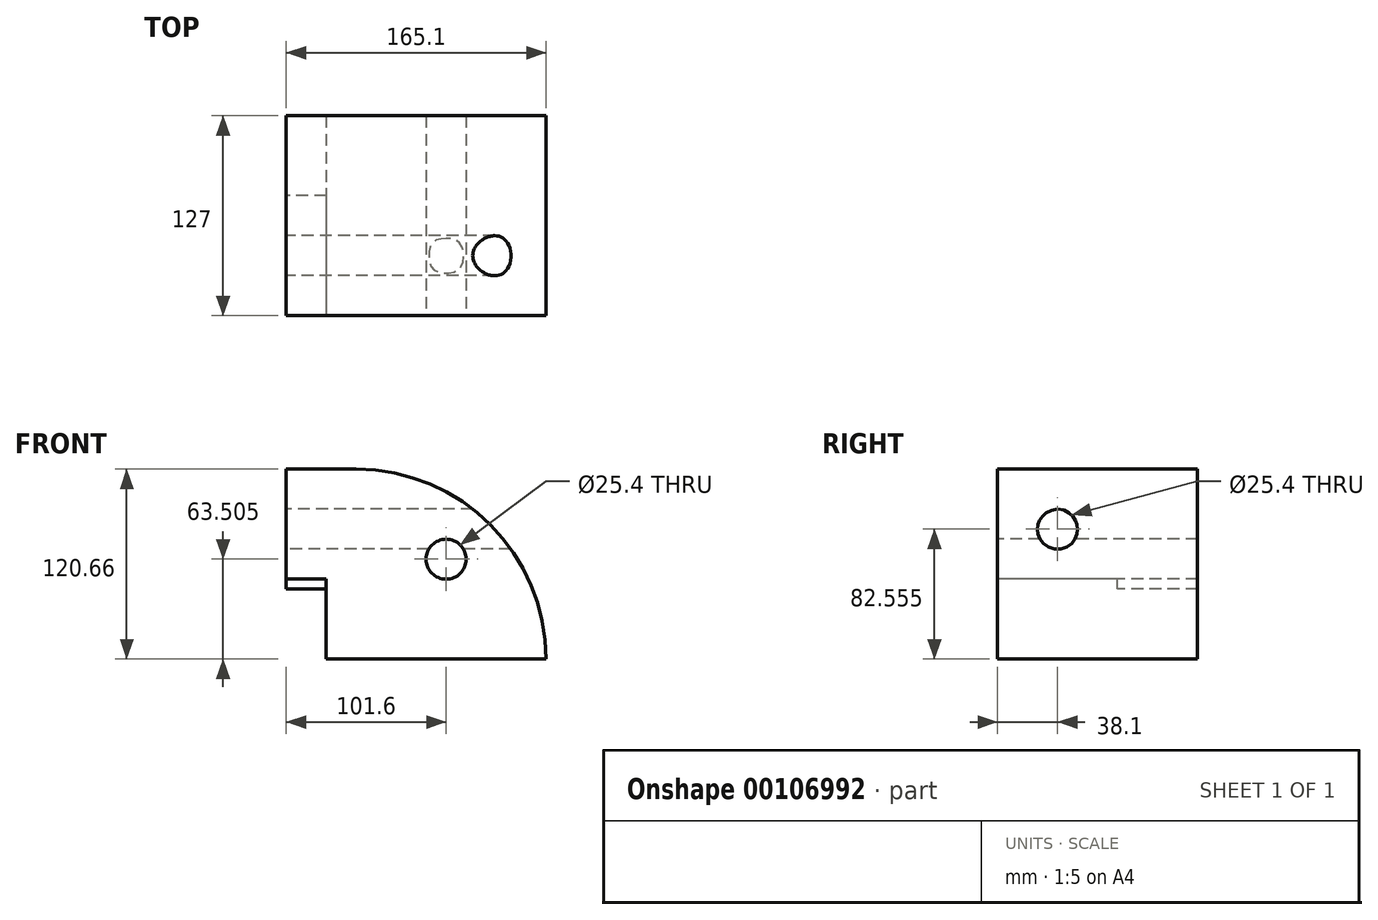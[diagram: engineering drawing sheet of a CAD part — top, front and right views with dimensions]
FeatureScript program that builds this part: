
annotation { "Feature Type Name" : "Feature", "Feature Type Description" : "" }
export const myFeature = defineFeature(function(context is Context, id is Id, definition is map)
    precondition{}
    {
        {
            var Q0;
            Q0=qCreatedBy(makeId("Right.planeOp"),FACE);
            var sketch = newSketch(context, id + "F0", { "sketchPlane" : qUnion([Q0])});
            skLineSegment(sketch, "E0.bottom", {"start": v(-63.5, 60.33) * mm, "end": v(63.5, 60.33) * mm});
            skLineSegment(sketch, "E0.top", {"start": v(-63.5, -60.33) * mm, "end": v(63.5, -60.33) * mm});
            skLineSegment(sketch, "E0.left", {"start": v(-63.5, 60.33) * mm, "end": v(-63.5, -60.33) * mm});
            skLineSegment(sketch, "E0.right", {"start": v(63.5, 60.32) * mm, "end": v(63.5, -60.33) * mm});
            skPoint(sketch, "E0.middle", {"position": v(0, 0) * mm});
            skSolve(sketch);
        }
        {
            var Q0;
            Q0=makeQuery(id+"F0.imprint","IMPRINT",FACE,{"disambiguationData":[TD([[makeQuery(id+"F0.imprint","IMPRINT",EDGE,{"derivedFrom":sQuery(id+"F0.wireOp",EDGE,"E0.bottom")}),-1.0]])]});
            extrude(context, id + "F1", {"entities" : qUnion([Q0]), "depth" : 215.9 * mm});
        }
        {
            var Q0;
            Q0=makeQuery(id+"F1.opExtrude","SWEPT_FACE",FACE,{"disambiguationData":[OSD([sQuery(id+"F0.wireOp",EDGE,"E0.left")])]});
            var sketch = newSketch(context, id + "F2", { "sketchPlane" : qUnion([Q0])});
            skLineSegment(sketch, "E1.bottom", {"start": v(0, -60.33) * mm, "end": v(76.2, -60.33) * mm});
            skLineSegment(sketch, "E1.top", {"start": v(0, -15.88) * mm, "end": v(76.2, -15.88) * mm});
            skLineSegment(sketch, "E1.left", {"start": v(0, -60.33) * mm, "end": v(0, -15.88) * mm});
            skLineSegment(sketch, "E1.right", {"start": v(76.2, -60.33) * mm, "end": v(76.2, -15.88) * mm});
            skSolve(sketch);
        }
        {
            var Q0;
            Q0=makeQuery(id+"F2.imprint","IMPRINT",FACE,{"disambiguationData":[TD([[makeQuery(id+"F2.imprint","IMPRINT",EDGE,{"derivedFrom":sQuery(id+"F2.wireOp",EDGE,"E1.bottom")}),-1.0]])]});
            extrude(context, id + "F3", {"entities" : qUnion([Q0]), "operationType" : NewBodyOperationType.REMOVE, "oppositeDirection" : true, "depth" : 127 * mm});
        }
        {
            var Q0;
            Q0=makeQuery(id+"F1.opExtrude","CAP_FACE",FACE,{"disambiguationData":[OSD([sQuery(id+"F0.wireOp",EDGE,"E0.bottom"),sQuery(id+"F0.wireOp",EDGE,"E0.top"),sQuery(id+"F0.wireOp",EDGE,"E0.left"),sQuery(id+"F0.wireOp",EDGE,"E0.right")])],"isStart":true});
            var sketch = newSketch(context, id + "F4", { "sketchPlane" : qUnion([Q0])});
            skLineSegment(sketch, "E2.bottom", {"start": v(-63.5, 60.32) * mm, "end": v(-12.7, 60.32) * mm});
            skLineSegment(sketch, "E2.top", {"start": v(-63.5, -15.88) * mm, "end": v(-12.7, -15.88) * mm});
            skLineSegment(sketch, "E2.left", {"start": v(-63.5, 60.32) * mm, "end": v(-63.5, -15.88) * mm});
            skLineSegment(sketch, "E2.right", {"start": v(-12.7, 60.32) * mm, "end": v(-12.7, -15.88) * mm});
            skLineSegment(sketch, "E3.bottom", {"start": v(-63.5, -15.88) * mm, "end": v(63.5, -15.88) * mm});
            skLineSegment(sketch, "E3.top", {"start": v(-63.5, -15.88) * mm, "end": v(63.5, -15.88) * mm});
            skLineSegment(sketch, "E3.left", {"start": v(-63.5, -15.88) * mm, "end": v(-63.5, -15.88) * mm});
            skLineSegment(sketch, "E3.right", {"start": v(63.5, -15.88) * mm, "end": v(63.5, -15.87) * mm});
            skSolve(sketch);
        }
        {
            var Q0;
            Q0=makeQuery(id+"F4.imprint","IMPRINT",FACE,{"disambiguationData":[TD([[makeQuery(id+"F4.imprint","IMPRINT",EDGE,{"derivedFrom":sQuery(id+"F4.wireOp",EDGE,"E2.bottom")}),1.0]])]});
            extrude(context, id + "F5", {"entities" : qUnion([Q0]), "operationType" : NewBodyOperationType.REMOVE, "oppositeDirection" : true, "depth" : 50.8 * mm});
        }
        {
            var Q0;
            Q0=makeQuery(id+"F1.opExtrude","CAP_FACE",FACE,{"disambiguationData":[OSD([sQuery(id+"F0.wireOp",EDGE,"E0.bottom"),sQuery(id+"F0.wireOp",EDGE,"E0.top"),sQuery(id+"F0.wireOp",EDGE,"E0.left"),sQuery(id+"F0.wireOp",EDGE,"E0.right")])],"isStart":true});
            var sketch = newSketch(context, id + "F6", { "sketchPlane" : qUnion([Q0])});
            skCircle(sketch, "E4", {"center": v(25.4, 22.22) * mm, "radius": 12.7 * mm});
            skSolve(sketch);
        }
        {
            var Q0;
            Q0=makeQuery(id+"F1.opExtrude","SWEPT_FACE",FACE,{"disambiguationData":[OSD([sQuery(id+"F0.wireOp",EDGE,"E0.left")])]});
            var sketch = newSketch(context, id + "F7", { "sketchPlane" : qUnion([Q0])});
            skLineSegment(sketch, "E5.bottom", {"start": v(215.9, -60.33) * mm, "end": v(141.2, -60.33) * mm});
            skLineSegment(sketch, "E5.left", {"start": v(215.9, -60.33) * mm, "end": v(215.9, -8.03) * mm});
            skPoint(sketch, "E6", {"position": v(152.4, 3.17) * mm});
            skSolve(sketch);
        }
        {
            var Q0;
            Q0=sQuery(id+"F7.wireOp",VERTEX,"E6");
            var Q1;
            Q1=makeQuery(id+"F1.opExtrude","SWEPT_BODY",BODY,{"disambiguationData":[OSD([sQuery(id+"F0.wireOp",EDGE,"E0.bottom"),sQuery(id+"F0.wireOp",EDGE,"E0.top"),sQuery(id+"F0.wireOp",EDGE,"E0.left"),sQuery(id+"F0.wireOp",EDGE,"E0.right")])]});
            hole(context, id + "F8", {"style" : HoleStyle.SIMPLE, "endStyle" : HoleEndStyle.BLIND, "holeDiameter" : 25.4 * mm, "holeDepth" : 127 * mm, "locations" : qUnion([Q0]), "scope" : qUnion([Q1])});
        }
        {
            var Q0;
            Q0=makeQuery(id+"F1.opExtrude","CAP_EDGE",EDGE,{"disambiguationData":[OSD([sQuery(id+"F0.wireOp",EDGE,"E0.bottom")])],"isStart":false});
            fillet(context, id + "F9", {"entities" : qUnion([Q0]), "radius" : 120.65 * mm, "tangentPropagation" : true, "allowEdgeOverflow" : false});
        }
        {
            var Q0;
            Q0=makeQuery(id+"F4.imprint","IMPRINT",FACE,{"disambiguationData":[TD([[makeQuery(id+"F4.imprint","IMPRINT",EDGE,{"derivedFrom":sQuery(id+"F4.wireOp",EDGE,"E3.bottom")}),1.0]])]});
            extrude(context, id + "F10", {"entities" : qUnion([Q0]), "operationType" : NewBodyOperationType.REMOVE, "oppositeDirection" : true, "depth" : 50.8 * mm});
        }
        {
            var Q0;
            {var subQ0=sQuery(id+"F4.wireOp",EDGE,"E3.top");Q0=makeQuery(id+"F10.boolean.opBoolean","MERGE",FACE,{"derivedFrom":[makeQuery(id+"F5.boolean.opBoolean","COPY",FACE,{"derivedFrom":makeQuery(id+"F5.opExtrude","CAP_FACE",FACE,{"disambiguationData":[OSD([sQuery(id+"F4.wireOp",EDGE,"E2.bottom"),sQuery(id+"F4.wireOp",EDGE,"E2.left"),sQuery(id+"F4.wireOp",EDGE,"E2.right"),subQ0])],"isStart":false})}),makeQuery(id+"F10.opExtrude","CAP_FACE",FACE,{"disambiguationData":[OSD([sQuery(id+"F4.wireOp",EDGE,"E3.bottom"),subQ0,sQuery(id+"F4.wireOp",EDGE,"E3.left"),sQuery(id+"F4.wireOp",EDGE,"E3.right")])],"isStart":false})]});}
            var sketch = newSketch(context, id + "F11", { "sketchPlane" : qUnion([Q0])});
            skLineSegment(sketch, "E7.bottom", {"start": v(-12.7, -15.88) * mm, "end": v(63.5, -15.88) * mm});
            skLineSegment(sketch, "E7.top", {"start": v(-12.7, -9.53) * mm, "end": v(63.5, -9.53) * mm});
            skLineSegment(sketch, "E7.left", {"start": v(-12.7, -15.88) * mm, "end": v(-12.7, -9.53) * mm});
            skLineSegment(sketch, "E7.right", {"start": v(63.5, -15.88) * mm, "end": v(63.5, -9.53) * mm});
            skSolve(sketch);
        }
        {
            var Q0;
            Q0=makeQuery(id+"F11.imprint","IMPRINT",FACE,{"disambiguationData":[TD([[makeQuery(id+"F11.imprint","IMPRINT",EDGE,{"derivedFrom":sQuery(id+"F11.wireOp",EDGE,"E7.bottom")}),1.0]])]});
            extrude(context, id + "F12", {"entities" : qUnion([Q0]), "operationType" : NewBodyOperationType.REMOVE, "oppositeDirection" : true, "depth" : 25.4 * mm});
        }
        {
            var Q0;
            Q0=sQuery(id+"F6.wireOp",VERTEX,"E4.center");
            var Q1;
            Q1=makeQuery(id+"F1.opExtrude","SWEPT_BODY",BODY,{"disambiguationData":[OSD([sQuery(id+"F0.wireOp",EDGE,"E0.bottom"),sQuery(id+"F0.wireOp",EDGE,"E0.top"),sQuery(id+"F0.wireOp",EDGE,"E0.left"),sQuery(id+"F0.wireOp",EDGE,"E0.right")])]});
            hole(context, id + "F13", {"style" : HoleStyle.SIMPLE, "endStyle" : HoleEndStyle.THROUGH, "holeDiameter" : 25.4 * mm, "locations" : qUnion([Q0]), "scope" : qUnion([Q1]), "isTappedThrough" : true});
        }
    });
